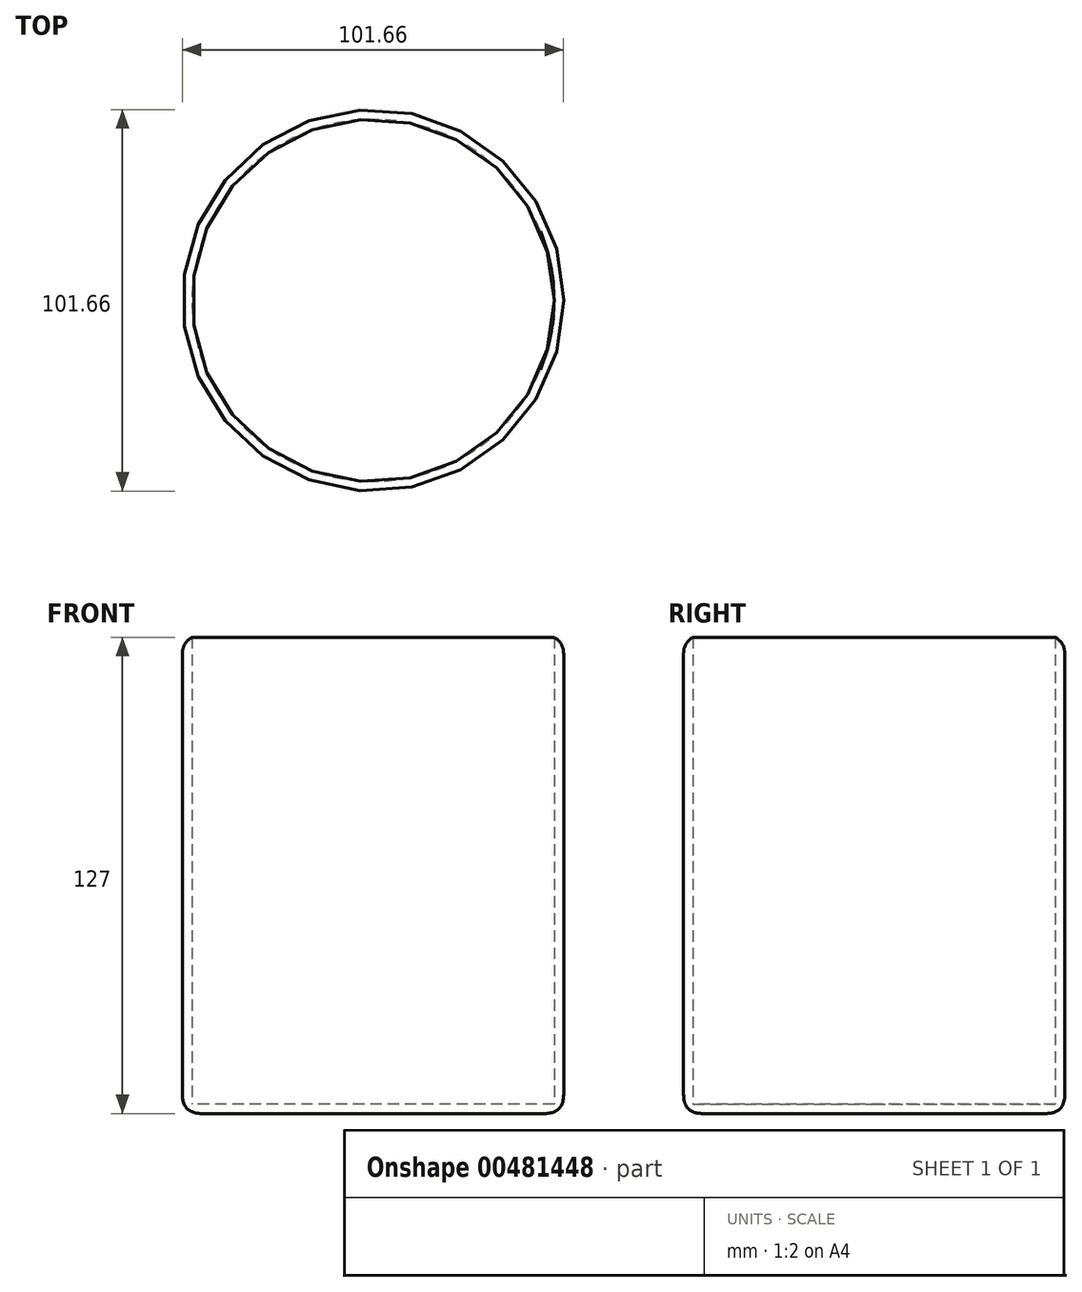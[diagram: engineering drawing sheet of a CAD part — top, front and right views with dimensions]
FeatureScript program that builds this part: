
annotation { "Feature Type Name" : "Feature", "Feature Type Description" : "" }
export const myFeature = defineFeature(function(context is Context, id is Id, definition is map)
    precondition{}
    {
        {
            var Q0;
            Q0=qCreatedBy(makeId("Top.planeOp"),FACE);
            var sketch = newSketch(context, id + "F0", { "sketchPlane" : qUnion([Q0])});
            skCircle(sketch, "E0", {"center": v(0, 0) * mm, "radius": 50.83 * mm});
            skSolve(sketch);
        }
        {
            var Q0;
            Q0=makeQuery(id+"F0.imprint","IMPRINT",FACE,{"disambiguationData":[TD([[makeQuery(id+"F0.imprint","IMPRINT",EDGE,{"derivedFrom":sQuery(id+"F0.wireOp",EDGE,"E0")}),1.0]])]});
            extrude(context, id + "F1", {"entities" : qUnion([Q0]), "depth" : 127 * mm});
        }
        {
            var Q0;
            Q0=makeQuery(id+"F1.opExtrude","CAP_FACE",FACE,{"disambiguationData":[OSD([sQuery(id+"F0.wireOp",EDGE,"E0")])],"isStart":false});
            shell(context, id + "F2", {"entities" : qUnion([Q0]), "thickness" : 2.54 * mm});
        }
        {
            var Q0;
            Q0=makeQuery(id+"F1.opExtrude","SWEPT_FACE",FACE,{"disambiguationData":[OSD([sQuery(id+"F0.wireOp",EDGE,"E0")])]});
            fillet(context, id + "F3", {"entities" : qUnion([Q0]), "radius" : 5.08 * mm, "tangentPropagation" : true, "rho" : 0.5, "crossSection" : FilletCrossSection.CONIC, "allowEdgeOverflow" : false});
        }
    });
